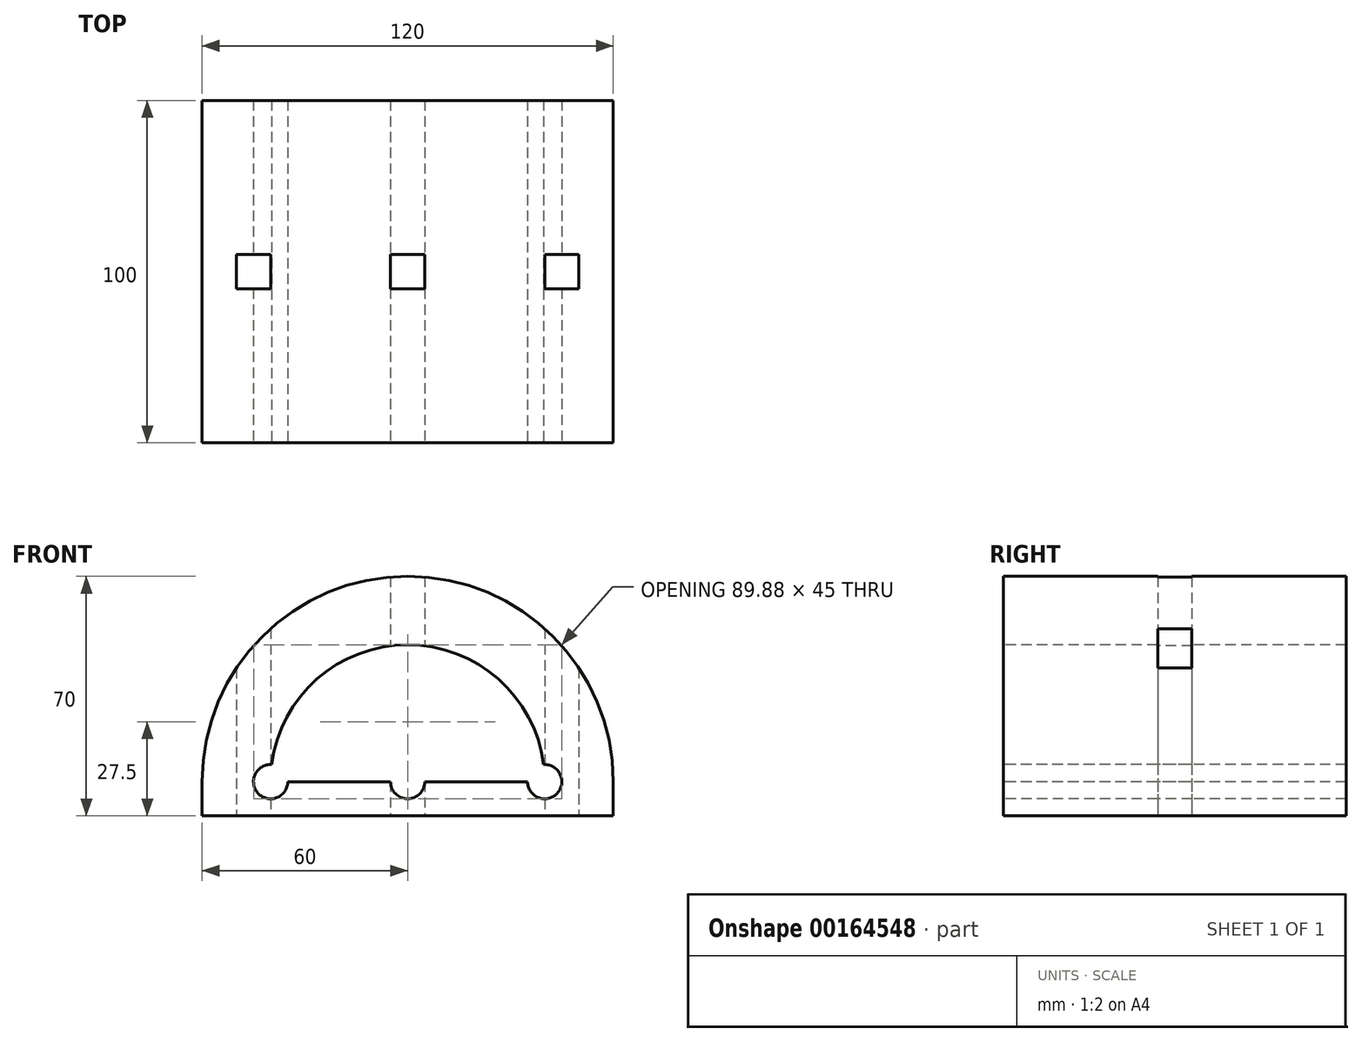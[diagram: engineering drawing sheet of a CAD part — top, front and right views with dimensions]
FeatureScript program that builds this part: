
annotation { "Feature Type Name" : "Feature", "Feature Type Description" : "" }
export const myFeature = defineFeature(function(context is Context, id is Id, definition is map)
    precondition{}
    {
        {
            var Q0;
            Q0=qCreatedBy(makeId("Front.planeOp"),FACE);
            var sketch = newSketch(context, id + "F0", { "sketchPlane" : qUnion([Q0])});
            skArc(sketch, "E0", {"start": v(60, 0) * mm, "mid": v(0, 60) * mm, "end": v(-60, 0) * mm});
            skLineSegment(sketch, "E1", {"start": v(-60, 0) * mm, "end": v(60, 0) * mm});
            skLineSegment(sketch, "E2", {"start": v(-60, 0) * mm, "end": v(-60, -10) * mm});
            skLineSegment(sketch, "E3", {"start": v(60, 0) * mm, "end": v(60, -10) * mm});
            skLineSegment(sketch, "E4", {"start": v(-60, -10) * mm, "end": v(60, -10) * mm});
            skSolve(sketch);
        }
        {
            var Q0;
            Q0 = qSketchRegion(id + "F0", true);
            extrude(context, id + "F1", {"entities" : qUnion([Q0]), "depth" : 100 * mm});
        }
        {
            var Q0;
            Q0=makeQuery(id+"F1.opExtrude","CAP_FACE",FACE,{"disambiguationData":[OSD([sQuery(id+"F0.wireOp",EDGE,"E0"),sQuery(id+"F0.wireOp",EDGE,"E2"),sQuery(id+"F0.wireOp",EDGE,"E3"),sQuery(id+"F0.wireOp",EDGE,"E4")])],"isStart":false});
            var sketch = newSketch(context, id + "F2", { "sketchPlane" : qUnion([Q0])});
            skArc(sketch, "E5", {"start": v(39.69, 5) * mm, "mid": v(0, 40) * mm, "end": v(-39.69, 5) * mm});
            skLineSegment(sketch, "E6", {"start": v(-35, 0) * mm, "end": v(35, 0) * mm});
            skArc(sketch, "E7", {"start": v(-39.69, 5) * mm, "mid": v(-43.64, -3.42) * mm, "end": v(-35, 0) * mm});
            skArc(sketch, "E8", {"start": v(35, 0) * mm, "mid": v(43.64, -3.42) * mm, "end": v(39.69, 5) * mm});
            skCircle(sketch, "E9", {"center": v(0, 0) * mm, "radius": 5 * mm});
            skSolve(sketch);
        }
        {
            var Q0;
            Q0 = qSketchRegion(id + "F2", true);
            extrude(context, id + "F3", {"entities" : qUnion([Q0]), "operationType" : NewBodyOperationType.REMOVE, "endBound" : BoundingType.THROUGH_ALL, "oppositeDirection" : true, "depth" : 25 * mm});
        }
        {
            var Q0;
            Q0=makeQuery(id+"F1.opExtrude","SWEPT_FACE",FACE,{"disambiguationData":[OSD([sQuery(id+"F0.wireOp",EDGE,"E4")])]});
            var sketch = newSketch(context, id + "F4", { "sketchPlane" : qUnion([Q0])});
            skLineSegment(sketch, "E10.bottom", {"start": v(-40, 45) * mm, "end": v(-50, 45) * mm});
            skLineSegment(sketch, "E10.top", {"start": v(-40, 55) * mm, "end": v(-50, 55) * mm});
            skLineSegment(sketch, "E10.left", {"start": v(-40, 45) * mm, "end": v(-40, 55) * mm});
            skLineSegment(sketch, "E10.right", {"start": v(-50, 45) * mm, "end": v(-50, 55) * mm});
            skPoint(sketch, "E10.middle", {"position": v(-45, 50) * mm});
            skLineSegment(sketch, "E11.bottom", {"start": v(5, 55) * mm, "end": v(-5, 55) * mm});
            skLineSegment(sketch, "E11.top", {"start": v(5, 45) * mm, "end": v(-5, 45) * mm});
            skLineSegment(sketch, "E11.left", {"start": v(5, 55) * mm, "end": v(5, 45) * mm});
            skLineSegment(sketch, "E11.right", {"start": v(-5, 55) * mm, "end": v(-5, 45) * mm});
            skPoint(sketch, "E11.middle", {"position": v(0, 50) * mm});
            skPoint(sketch, "E11.middle.positionSnap0", {"position": v(60, 50) * mm});
            skPoint(sketch, "E11.centerSnap0", {"position": v(60, 50) * mm});
            skLineSegment(sketch, "E12.bottom", {"start": v(50, 55) * mm, "end": v(40, 55) * mm});
            skLineSegment(sketch, "E12.top", {"start": v(50, 45) * mm, "end": v(40, 45) * mm});
            skLineSegment(sketch, "E12.left", {"start": v(50, 55) * mm, "end": v(50, 45) * mm});
            skLineSegment(sketch, "E12.right", {"start": v(40, 55) * mm, "end": v(40, 45) * mm});
            skPoint(sketch, "E12.middle", {"position": v(45, 50) * mm});
            skSolve(sketch);
        }
        {
            var Q0;
            Q0 = qSketchRegion(id + "F4", true);
            extrude(context, id + "F5", {"entities" : qUnion([Q0]), "operationType" : NewBodyOperationType.REMOVE, "endBound" : BoundingType.THROUGH_ALL, "oppositeDirection" : true, "depth" : 25 * mm});
        }
    });
